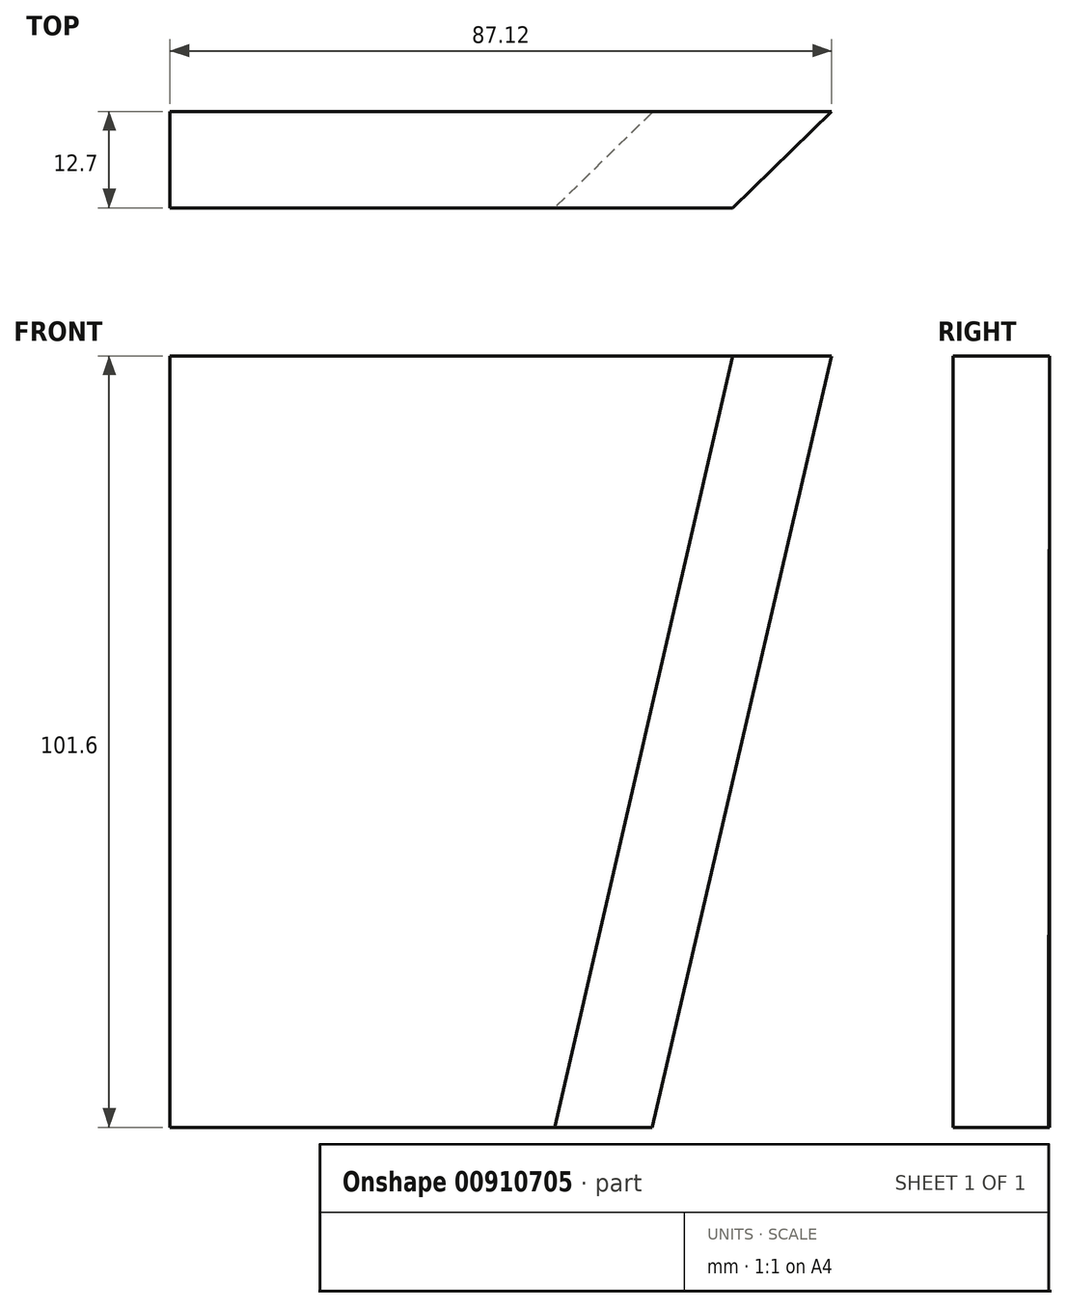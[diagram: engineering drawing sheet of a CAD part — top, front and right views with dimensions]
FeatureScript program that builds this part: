
annotation { "Feature Type Name" : "Feature", "Feature Type Description" : "" }
export const myFeature = defineFeature(function(context is Context, id is Id, definition is map)
    precondition{}
    {
        {
            var Q0;
            Q0=qCreatedBy(makeId("Front.planeOp"),FACE);
            var sketch = newSketch(context, id + "F0", { "sketchPlane" : qUnion([Q0])});
            skLineSegment(sketch, "E0", {"start": v(0, 0) * mm, "end": v(0, -101.6) * mm});
            skLineSegment(sketch, "E1", {"start": v(0, -101.6) * mm, "end": v(63.5, -101.6) * mm});
            skLineSegment(sketch, "E2", {"start": v(63.5, -101.6) * mm, "end": v(87.12, 0) * mm});
            skLineSegment(sketch, "E3", {"start": v(87.12, 0) * mm, "end": v(0, 0) * mm});
            skSolve(sketch);
        }
        {
            var Q0;
            Q0=makeQuery(id+"F0.imprint","IMPRINT",FACE,{"disambiguationData":[TD([[makeQuery(id+"F0.imprint","IMPRINT",EDGE,{"derivedFrom":sQuery(id+"F0.wireOp",EDGE,"E0")}),1.0]])]});
            extrude(context, id + "F1", {"entities" : qUnion([Q0]), "depth" : 12.7 * mm, "offsetDistance" : 25.4 * mm});
        }
        {
            var Q0;
            Q0=makeQuery(id+"F1.opExtrude","SWEPT_EDGE",EDGE,{"disambiguationData":[OSD([sQuery(id+"F0.wireOp",EDGE,"E2"),sQuery(id+"F0.wireOp",EDGE,"E3")])]});
            var Q1;
            Q1=makeQuery(id+"F1.opExtrude","SWEPT_FACE",FACE,{"disambiguationData":[OSD([sQuery(id+"F0.wireOp",EDGE,"E3")])]});
            cPlane(context, id + "F2", {"entities" : qUnion([Q0, Q1]), "cplaneType" : CPlaneType.LINE_ANGLE, "offset" : 25.4 * mm, "angle" : 13 * degree, "width" : 152.4 * mm, "height" : 152.4 * mm});
        }
        {
            var Q0;
            Q0=qCreatedBy(id+"F2.planeOp",FACE);
            var sketch = newSketch(context, id + "F3", { "sketchPlane" : qUnion([Q0])});
            skLineSegment(sketch, "E4", {"start": v(72.19, 12.7) * mm, "end": v(84.89, 12.7) * mm});
            skLineSegment(sketch, "E5", {"start": v(84.89, 12.7) * mm, "end": v(84.89, 0) * mm});
            skLineSegment(sketch, "E6", {"start": v(84.89, 0) * mm, "end": v(72.19, 12.7) * mm});
            skSolve(sketch);
        }
        {
            var Q0;
            Q0=makeQuery(id+"F3.imprint","IMPRINT",FACE,{"disambiguationData":[TD([[makeQuery(id+"F3.imprint","IMPRINT",EDGE,{"derivedFrom":sQuery(id+"F3.wireOp",EDGE,"E4")}),-1.0]])]});
            extrude(context, id + "F4", {"entities" : qUnion([Q0]), "operationType" : NewBodyOperationType.REMOVE, "endBound" : BoundingType.THROUGH_ALL, "depth" : 12700 * mm, "offsetDistance" : 25.4 * mm});
        }
    });
